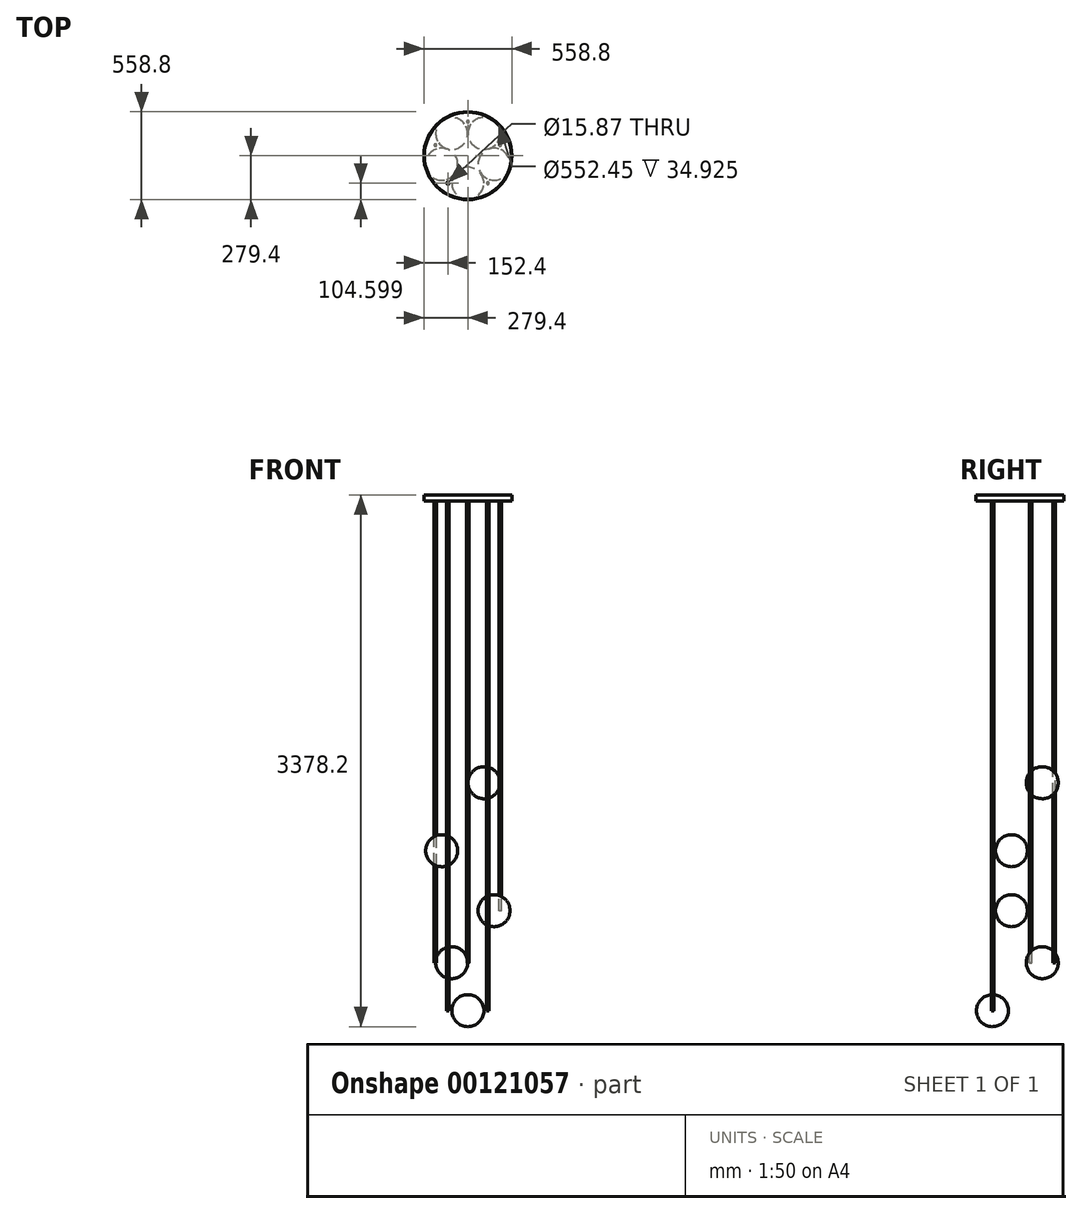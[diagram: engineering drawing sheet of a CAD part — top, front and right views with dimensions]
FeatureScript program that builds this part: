
annotation { "Feature Type Name" : "Feature", "Feature Type Description" : "" }
export const myFeature = defineFeature(function(context is Context, id is Id, definition is map)
    precondition{}
    {
        {
            var Q0;
            Q0=qCreatedBy(makeId("Front.planeOp"),FACE);
            var sketch = newSketch(context, id + "F0", { "sketchPlane" : qUnion([Q0])});
            skLineSegment(sketch, "E0", {"start": v(0, 0) * mm, "end": v(5560.38, 0) * mm, "construction": true});
            skCircle(sketch, "E1", {"center": v(0, 2108.2) * mm, "radius": 127 * mm});
            skLineSegment(sketch, "E2", {"start": v(0, 2235.2) * mm, "end": v(0, 4203.7) * mm});
            skLineSegment(sketch, "E3.bottom", {"start": v(0, 2540) * mm, "end": v(812.8, 2540) * mm});
            skLineSegment(sketch, "E3.top", {"start": v(0, 2489.2) * mm, "end": v(812.8, 2489.2) * mm});
            skLineSegment(sketch, "E3.left", {"start": v(0, 2540) * mm, "end": v(0, 2489.2) * mm});
            skLineSegment(sketch, "E3.right", {"start": v(812.8, 2540) * mm, "end": v(812.8, 2489.2) * mm});
            skLineSegment(sketch, "E4", {"start": v(812.8, 4203.7) * mm, "end": v(812.8, 1930.4) * mm});
            skCircle(sketch, "E5", {"center": v(939.8, 1930.4) * mm, "radius": 101.6 * mm});
            skLineSegment(sketch, "E6", {"start": v(1066.8, 4203.7) * mm, "end": v(1066.8, 1397) * mm});
            skLineSegment(sketch, "E7", {"start": v(812.8, 4203.7) * mm, "end": v(1066.8, 4203.7) * mm});
            skPoint(sketch, "E8", {"position": v(939.8, 4203.7) * mm});
            skCircle(sketch, "E9", {"center": v(939.8, 2819.4) * mm, "radius": 101.6 * mm});
            skCircle(sketch, "E10", {"center": v(1066.8, 1270) * mm, "radius": 127 * mm});
            skLineSegment(sketch, "E11.bottom", {"start": v(1066.8, 1701.8) * mm, "end": v(1879.6, 1701.8) * mm});
            skLineSegment(sketch, "E11.top", {"start": v(1066.8, 1651) * mm, "end": v(1879.6, 1651) * mm});
            skLineSegment(sketch, "E11.left", {"start": v(1066.8, 1701.8) * mm, "end": v(1066.8, 1651) * mm});
            skLineSegment(sketch, "E11.right", {"start": v(1879.6, 1701.8) * mm, "end": v(1879.6, 1651) * mm});
            skLineSegment(sketch, "E12", {"start": v(1879.6, 1651) * mm, "end": v(1879.6, 4203.7) * mm});
            skLineSegment(sketch, "E13", {"start": v(1879.6, 4203.7) * mm, "end": v(2133.6, 4203.7) * mm});
            skLineSegment(sketch, "E14", {"start": v(2133.6, 4203.7) * mm, "end": v(2133.6, 2362.2) * mm});
            skCircle(sketch, "E15", {"center": v(2006.6, 2362.2) * mm, "radius": 101.6 * mm});
            skPoint(sketch, "E15.centerSnap0", {"position": v(2006.6, 4203.7) * mm});
            skLineSegment(sketch, "E16", {"start": v(0, 4203.7) * mm, "end": v(0, 4267.2) * mm});
            skLineSegment(sketch, "E17", {"start": v(939.8, 2819.4) * mm, "end": v(812.8, 2819.4) * mm, "construction": true});
            skLineSegment(sketch, "E18", {"start": v(812.8, 2794) * mm, "end": v(939.8, 2794) * mm, "construction": true});
            skSolve(sketch);
        }
        {
            var Q0;
            Q0=qCreatedBy(makeId("Front.planeOp"),FACE);
            var sketch = newSketch(context, id + "F1", { "sketchPlane" : qUnion([Q0])});
            skLineSegment(sketch, "E19.0", {"start": v(0, 0) * mm, "end": v(5560.38, 0) * mm});
            skCircle(sketch, "E19.1", {"center": v(0, 2108.2) * mm, "radius": 127 * mm, "construction": true});
            skLineSegment(sketch, "E19.2", {"start": v(0, 2235.2) * mm, "end": v(0, 4203.7) * mm, "construction": true});
            skLineSegment(sketch, "E19.3", {"start": v(0, 2540) * mm, "end": v(812.8, 2540) * mm, "construction": true});
            skLineSegment(sketch, "E19.4", {"start": v(0, 2489.2) * mm, "end": v(812.8, 2489.2) * mm, "construction": true});
            skLineSegment(sketch, "E19.5", {"start": v(0, 2540) * mm, "end": v(0, 2489.2) * mm, "construction": true});
            skLineSegment(sketch, "E19.6", {"start": v(812.8, 2540) * mm, "end": v(812.8, 2489.2) * mm, "construction": true});
            skLineSegment(sketch, "E19.7", {"start": v(812.8, 4203.7) * mm, "end": v(812.8, 1930.4) * mm, "construction": true});
            skCircle(sketch, "E19.8", {"center": v(939.8, 1930.4) * mm, "radius": 101.6 * mm, "construction": true});
            skLineSegment(sketch, "E19.9", {"start": v(1066.8, 4203.7) * mm, "end": v(1066.8, 1397) * mm, "construction": true});
            skLineSegment(sketch, "E19.10", {"start": v(812.8, 4203.7) * mm, "end": v(1066.8, 4203.7) * mm, "construction": true});
            skPoint(sketch, "E19.11", {"position": v(939.8, 4203.7) * mm});
            skCircle(sketch, "E19.12", {"center": v(939.8, 2819.4) * mm, "radius": 101.6 * mm, "construction": true});
            skCircle(sketch, "E19.13", {"center": v(1066.8, 1270) * mm, "radius": 127 * mm, "construction": true});
            skLineSegment(sketch, "E19.14", {"start": v(1066.8, 1701.8) * mm, "end": v(1879.6, 1701.8) * mm, "construction": true});
            skLineSegment(sketch, "E19.15", {"start": v(1066.8, 1651) * mm, "end": v(1879.6, 1651) * mm, "construction": true});
            skLineSegment(sketch, "E19.16", {"start": v(1066.8, 1701.8) * mm, "end": v(1066.8, 1651) * mm, "construction": true});
            skLineSegment(sketch, "E19.17", {"start": v(1879.6, 1701.8) * mm, "end": v(1879.6, 1651) * mm, "construction": true});
            skLineSegment(sketch, "E19.18", {"start": v(1879.6, 1651) * mm, "end": v(1879.6, 4203.7) * mm, "construction": true});
            skLineSegment(sketch, "E19.19", {"start": v(1879.6, 4203.7) * mm, "end": v(2133.6, 4203.7) * mm, "construction": true});
            skLineSegment(sketch, "E19.20", {"start": v(2133.6, 4203.7) * mm, "end": v(2133.6, 2362.2) * mm, "construction": true});
            skCircle(sketch, "E19.21", {"center": v(2006.6, 2362.2) * mm, "radius": 101.6 * mm, "construction": true});
            skPoint(sketch, "E19.22", {"position": v(2006.6, 4203.7) * mm});
            skPoint(sketch, "E20.middle", {"position": v(0, 3219.45) * mm});
            skLineSegment(sketch, "E21.bottom", {"start": v(804.86, 4203.7) * mm, "end": v(820.74, 4203.7) * mm});
            skLineSegment(sketch, "E21.top", {"start": v(804.86, 2844.8) * mm, "end": v(820.74, 2844.8) * mm});
            skLineSegment(sketch, "E21.left", {"start": v(804.86, 4203.7) * mm, "end": v(804.86, 2844.8) * mm});
            skLineSegment(sketch, "E21.right", {"start": v(820.74, 4203.7) * mm, "end": v(820.74, 2844.8) * mm});
            skPoint(sketch, "E21.middle", {"position": v(812.8, 3524.25) * mm});
            skLineSegment(sketch, "E22.bottom", {"start": v(804.86, 2794) * mm, "end": v(820.74, 2794) * mm});
            skLineSegment(sketch, "E22.top", {"start": v(804.86, 2540) * mm, "end": v(820.74, 2540) * mm});
            skLineSegment(sketch, "E22.left", {"start": v(804.86, 2794) * mm, "end": v(804.86, 2540) * mm});
            skLineSegment(sketch, "E22.right", {"start": v(820.74, 2794) * mm, "end": v(820.74, 2540) * mm});
            skPoint(sketch, "E22.middle", {"position": v(812.8, 2667) * mm});
            skLineSegment(sketch, "E23", {"start": v(812.8, 2514.6) * mm, "end": v(0, 2514.6) * mm, "construction": true});
            skLineSegment(sketch, "E24.bottom", {"start": v(804.86, 2489.2) * mm, "end": v(820.74, 2489.2) * mm});
            skLineSegment(sketch, "E24.top", {"start": v(804.86, 1955.8) * mm, "end": v(820.74, 1955.8) * mm});
            skLineSegment(sketch, "E24.left", {"start": v(804.86, 2489.2) * mm, "end": v(804.86, 1955.8) * mm});
            skLineSegment(sketch, "E24.right", {"start": v(820.74, 2489.2) * mm, "end": v(820.74, 1955.8) * mm});
            skPoint(sketch, "E24.middle", {"position": v(812.8, 2222.5) * mm});
            skLineSegment(sketch, "E25", {"start": v(939.8, 1930.4) * mm, "end": v(812.8, 1930.4) * mm, "construction": true});
            skLineSegment(sketch, "E26", {"start": v(939.8, 1930.4) * mm, "end": v(1066.8, 1930.4) * mm, "construction": true});
            skLineSegment(sketch, "E27.bottom", {"start": v(1058.86, 4203.7) * mm, "end": v(1074.74, 4203.7) * mm});
            skLineSegment(sketch, "E27.top", {"start": v(1058.86, 2844.8) * mm, "end": v(1074.74, 2844.8) * mm});
            skLineSegment(sketch, "E27.left", {"start": v(1058.86, 4203.7) * mm, "end": v(1058.86, 2844.8) * mm});
            skLineSegment(sketch, "E27.right", {"start": v(1074.74, 4203.7) * mm, "end": v(1074.74, 2844.8) * mm});
            skPoint(sketch, "E27.middle", {"position": v(1066.8, 3524.25) * mm});
            skLineSegment(sketch, "E28.bottom", {"start": v(1058.86, 2794) * mm, "end": v(1074.74, 2794) * mm});
            skLineSegment(sketch, "E28.top", {"start": v(1058.86, 1955.8) * mm, "end": v(1074.74, 1955.8) * mm});
            skLineSegment(sketch, "E28.left", {"start": v(1058.86, 2794) * mm, "end": v(1058.86, 1955.8) * mm});
            skLineSegment(sketch, "E28.right", {"start": v(1074.74, 2794) * mm, "end": v(1074.74, 1955.8) * mm});
            skPoint(sketch, "E28.middle", {"position": v(1066.8, 2374.9) * mm});
            skLineSegment(sketch, "E29.bottom", {"start": v(1058.86, 1905) * mm, "end": v(1074.74, 1905) * mm});
            skLineSegment(sketch, "E29.top", {"start": v(1058.86, 1701.8) * mm, "end": v(1074.74, 1701.8) * mm});
            skLineSegment(sketch, "E29.left", {"start": v(1058.86, 1905) * mm, "end": v(1058.86, 1701.8) * mm});
            skLineSegment(sketch, "E29.right", {"start": v(1074.74, 1905) * mm, "end": v(1074.74, 1701.8) * mm});
            skPoint(sketch, "E29.middle", {"position": v(1066.8, 1803.4) * mm});
            skLineSegment(sketch, "E30", {"start": v(1066.8, 1676.4) * mm, "end": v(1879.6, 1676.4) * mm, "construction": true});
            skLineSegment(sketch, "E31.bottom", {"start": v(1058.86, 1651) * mm, "end": v(1074.74, 1651) * mm});
            skLineSegment(sketch, "E31.top", {"start": v(1058.86, 1397) * mm, "end": v(1074.74, 1397) * mm});
            skLineSegment(sketch, "E31.left", {"start": v(1058.86, 1651) * mm, "end": v(1058.86, 1397) * mm});
            skLineSegment(sketch, "E31.right", {"start": v(1074.74, 1651) * mm, "end": v(1074.74, 1397) * mm});
            skPoint(sketch, "E31.middle", {"position": v(1066.8, 1524) * mm});
            skLineSegment(sketch, "E32.bottom", {"start": v(1871.66, 4203.7) * mm, "end": v(1887.54, 4203.7) * mm});
            skLineSegment(sketch, "E32.top", {"start": v(1871.66, 2387.6) * mm, "end": v(1887.54, 2387.6) * mm});
            skLineSegment(sketch, "E32.left", {"start": v(1871.66, 4203.7) * mm, "end": v(1871.66, 2387.6) * mm});
            skLineSegment(sketch, "E32.right", {"start": v(1887.54, 4203.7) * mm, "end": v(1887.54, 2387.6) * mm});
            skPoint(sketch, "E32.middle", {"position": v(1879.6, 3295.65) * mm});
            skLineSegment(sketch, "E33.bottom", {"start": v(1871.66, 2336.8) * mm, "end": v(1887.54, 2336.8) * mm});
            skLineSegment(sketch, "E33.top", {"start": v(1871.66, 1701.8) * mm, "end": v(1887.54, 1701.8) * mm});
            skLineSegment(sketch, "E33.left", {"start": v(1871.66, 2336.8) * mm, "end": v(1871.66, 1701.8) * mm});
            skLineSegment(sketch, "E33.right", {"start": v(1887.54, 2336.8) * mm, "end": v(1887.54, 1701.8) * mm});
            skPoint(sketch, "E33.middle", {"position": v(1879.6, 2019.3) * mm});
            skLineSegment(sketch, "E34.bottom", {"start": v(2125.66, 4203.7) * mm, "end": v(2141.54, 4203.7) * mm});
            skLineSegment(sketch, "E34.top", {"start": v(2125.66, 2387.6) * mm, "end": v(2141.54, 2387.6) * mm});
            skLineSegment(sketch, "E34.left", {"start": v(2125.66, 4203.7) * mm, "end": v(2125.66, 2387.6) * mm});
            skLineSegment(sketch, "E34.right", {"start": v(2141.54, 4203.7) * mm, "end": v(2141.54, 2387.6) * mm});
            skPoint(sketch, "E34.middle", {"position": v(2133.6, 3295.65) * mm});
            skLineSegment(sketch, "E35.bottom", {"start": v(7.94, 4203.7) * mm, "end": v(-7.94, 4203.7) * mm});
            skLineSegment(sketch, "E35.top", {"start": v(7.94, 2540) * mm, "end": v(-7.94, 2540) * mm});
            skLineSegment(sketch, "E35.left", {"start": v(7.94, 4203.7) * mm, "end": v(7.94, 2540) * mm});
            skLineSegment(sketch, "E35.right", {"start": v(-7.94, 4203.7) * mm, "end": v(-7.94, 2540) * mm});
            skPoint(sketch, "E35.middle", {"position": v(0, 3371.85) * mm});
            skLineSegment(sketch, "E36.bottom", {"start": v(-7.94, 2489.2) * mm, "end": v(7.94, 2489.2) * mm});
            skLineSegment(sketch, "E36.top", {"start": v(-7.94, 2235.2) * mm, "end": v(7.94, 2235.2) * mm});
            skLineSegment(sketch, "E36.left", {"start": v(-7.94, 2489.2) * mm, "end": v(-7.94, 2235.2) * mm});
            skLineSegment(sketch, "E36.right", {"start": v(7.94, 2489.2) * mm, "end": v(7.94, 2235.2) * mm});
            skPoint(sketch, "E36.middle", {"position": v(0, 2362.2) * mm});
            skSolve(sketch);
        }
        {
            var Q0;
            Q0=qCreatedBy(makeId("Front.planeOp"),FACE);
            var sketch = newSketch(context, id + "F2", { "sketchPlane" : qUnion([Q0])});
            skLineSegment(sketch, "E37.0", {"start": v(0, 0) * mm, "end": v(5560.38, 0) * mm, "construction": true});
            skCircle(sketch, "E38", {"center": v(4419.6, 1524) * mm, "radius": 127 * mm, "construction": true});
            skLineSegment(sketch, "E39", {"start": v(4419.6, 1651) * mm, "end": v(4419.6, 4203.7) * mm, "construction": true});
            skLineSegment(sketch, "E40.0", {"start": v(1879.6, 4203.7) * mm, "end": v(2133.6, 4203.7) * mm, "construction": true});
            skLineSegment(sketch, "E41", {"start": v(4673.6, 4203.7) * mm, "end": v(4673.6, 2133.6) * mm, "construction": true});
            skLineSegment(sketch, "E42", {"start": v(4419.6, 4203.7) * mm, "end": v(4673.6, 4203.7) * mm, "construction": true});
            skCircle(sketch, "E43", {"center": v(4546.6, 2133.6) * mm, "radius": 101.6 * mm, "construction": true});
            skPoint(sketch, "E43.centerSnap0", {"position": v(4546.6, 4203.7) * mm});
            skLineSegment(sketch, "E44.bottom", {"start": v(4411.66, 4203.7) * mm, "end": v(4427.54, 4203.7) * mm});
            skLineSegment(sketch, "E44.top", {"start": v(4411.66, 2159) * mm, "end": v(4427.54, 2159) * mm});
            skLineSegment(sketch, "E44.left", {"start": v(4411.66, 4203.7) * mm, "end": v(4411.66, 2159) * mm});
            skLineSegment(sketch, "E44.right", {"start": v(4427.54, 4203.7) * mm, "end": v(4427.54, 2159) * mm});
            skPoint(sketch, "E44.middle", {"position": v(4419.6, 3181.35) * mm});
            skLineSegment(sketch, "E45.bottom", {"start": v(4411.66, 2108.2) * mm, "end": v(4427.54, 2108.2) * mm});
            skLineSegment(sketch, "E45.top", {"start": v(4411.66, 1651) * mm, "end": v(4427.54, 1651) * mm});
            skLineSegment(sketch, "E45.left", {"start": v(4411.66, 2108.2) * mm, "end": v(4411.66, 1651) * mm});
            skLineSegment(sketch, "E45.right", {"start": v(4427.54, 2108.2) * mm, "end": v(4427.54, 1651) * mm});
            skPoint(sketch, "E45.middle", {"position": v(4419.6, 1879.6) * mm});
            skCircle(sketch, "E46.0", {"center": v(2006.6, 2362.2) * mm, "radius": 101.6 * mm, "construction": true});
            skLineSegment(sketch, "E47.bottom", {"start": v(4665.66, 4203.7) * mm, "end": v(4681.54, 4203.7) * mm});
            skLineSegment(sketch, "E47.top", {"start": v(4665.66, 2159) * mm, "end": v(4681.54, 2159) * mm});
            skLineSegment(sketch, "E47.left", {"start": v(4665.66, 4203.7) * mm, "end": v(4665.66, 2159) * mm});
            skLineSegment(sketch, "E47.right", {"start": v(4681.54, 4203.7) * mm, "end": v(4681.54, 2159) * mm});
            skPoint(sketch, "E47.middle", {"position": v(4673.6, 3181.35) * mm});
            skSolve(sketch);
        }
        {
            var Q0;
            Q0=qCreatedBy(makeId("Front.planeOp"),FACE);
            var sketch = newSketch(context, id + "F3", { "sketchPlane" : qUnion([Q0])});
            skLineSegment(sketch, "E48.0", {"start": v(0, 0) * mm, "end": v(5560.38, 0) * mm, "construction": true});
            skLineSegment(sketch, "E49", {"start": v(5560.38, 0) * mm, "end": v(9395.47, 0) * mm, "construction": true});
            skCircle(sketch, "E50", {"center": v(7086.6, 965.2) * mm, "radius": 101.6 * mm, "construction": true});
            skCircle(sketch, "E51.0", {"center": v(4419.6, 1524) * mm, "radius": 127 * mm, "construction": true});
            skLineSegment(sketch, "E52.0", {"start": v(4419.6, 4203.7) * mm, "end": v(4673.6, 4203.7) * mm, "construction": true});
            skLineSegment(sketch, "E53", {"start": v(7086.6, 965.2) * mm, "end": v(6959.6, 965.2) * mm, "construction": true});
            skLineSegment(sketch, "E54", {"start": v(6959.6, 965.2) * mm, "end": v(6959.6, 4203.7) * mm, "construction": true});
            skLineSegment(sketch, "E55", {"start": v(7213.6, 965.2) * mm, "end": v(7213.6, 4203.7) * mm, "construction": true});
            skLineSegment(sketch, "E56", {"start": v(6959.6, 4203.7) * mm, "end": v(7213.6, 4203.7) * mm, "construction": true});
            skPoint(sketch, "E57", {"position": v(7086.6, 4203.7) * mm});
            skLineSegment(sketch, "E58", {"start": v(6959.6, 4203.7) * mm, "end": v(6705.6, 4203.7) * mm, "construction": true});
            skLineSegment(sketch, "E59", {"start": v(6705.6, 4203.7) * mm, "end": v(6705.6, 1981.2) * mm, "construction": true});
            skCircle(sketch, "E60", {"center": v(6832.6, 1981.2) * mm, "radius": 101.6 * mm, "construction": true});
            skPoint(sketch, "E60.centerSnap0", {"position": v(6832.6, 4203.7) * mm});
            skLineSegment(sketch, "E61", {"start": v(6705.6, 4203.7) * mm, "end": v(6451.6, 4203.7) * mm, "construction": true});
            skLineSegment(sketch, "E62", {"start": v(6451.6, 4203.7) * mm, "end": v(6451.6, 1270) * mm, "construction": true});
            skCircle(sketch, "E63", {"center": v(6578.6, 1270) * mm, "radius": 101.6 * mm, "construction": true});
            skPoint(sketch, "E63.centerSnap0", {"position": v(6578.6, 4203.7) * mm});
            skLineSegment(sketch, "E64", {"start": v(7213.6, 4203.7) * mm, "end": v(7467.6, 4203.7) * mm, "construction": true});
            skLineSegment(sketch, "E65", {"start": v(7467.6, 4203.7) * mm, "end": v(7467.6, 1600.2) * mm, "construction": true});
            skLineSegment(sketch, "E66", {"start": v(7467.6, 4203.7) * mm, "end": v(7721.6, 4203.7) * mm});
            skLineSegment(sketch, "E67", {"start": v(7721.6, 4203.7) * mm, "end": v(7721.6, 2413) * mm, "construction": true});
            skCircle(sketch, "E68", {"center": v(7594.6, 2413) * mm, "radius": 101.6 * mm, "construction": true});
            skPoint(sketch, "E68.centerSnap0", {"position": v(7594.6, 4203.7) * mm});
            skCircle(sketch, "E69", {"center": v(7340.6, 1600.2) * mm, "radius": 101.6 * mm, "construction": true});
            skPoint(sketch, "E69.centerSnap0", {"position": v(7340.6, 4203.7) * mm});
            skLineSegment(sketch, "E70", {"start": v(6705.6, 1981.2) * mm, "end": v(6705.6, 1270) * mm, "construction": true});
            skLineSegment(sketch, "E71", {"start": v(7467.6, 2413) * mm, "end": v(7467.6, 1600.2) * mm, "construction": true});
            skLineSegment(sketch, "E72", {"start": v(7086.6, 863.6) * mm, "end": v(8026.4, 863.6) * mm, "construction": true});
            skLineSegment(sketch, "E73", {"start": v(8026.4, 863.6) * mm, "end": v(8026.4, 4203.7) * mm, "construction": true});
            skSolve(sketch);
        }
        {
            var Q0;
            Q0=qCreatedBy(makeId("Top.planeOp"),FACE);
            var Q1;
            Q1=sQuery(id+"F3.wireOp",VERTEX,"E57");
            cPlane(context, id + "F4", {"entities" : qUnion([Q0, Q1]), "cplaneType" : CPlaneType.PLANE_POINT, "offset" : 25.4 * mm, "width" : 152.4 * mm, "height" : 152.4 * mm});
        }
        {
            var Q0;
            Q0=qCreatedBy(id+"F4.planeOp",FACE);
            var sketch = newSketch(context, id + "F5", { "sketchPlane" : qUnion([Q0])});
            skPoint(sketch, "E74.0", {"position": v(7086.6, 0) * mm});
            skCircle(sketch, "E75.cCircle", {"center": v(7086.6, 0) * mm, "radius": 174.8 * mm, "construction": true});
            skLineSegment(sketch, "E75.0", {"start": v(7086.6, 216.07) * mm, "end": v(7292.1, 66.77) * mm});
            skLineSegment(sketch, "E75.1", {"start": v(7292.1, 66.77) * mm, "end": v(7213.6, -174.8) * mm});
            skLineSegment(sketch, "E75.2", {"start": v(7213.6, -174.8) * mm, "end": v(6959.6, -174.8) * mm});
            skLineSegment(sketch, "E75.3", {"start": v(6959.6, -174.8) * mm, "end": v(6881.1, 66.77) * mm});
            skLineSegment(sketch, "E75.4", {"start": v(6881.1, 66.77) * mm, "end": v(7086.6, 216.07) * mm});
            skPoint(sketch, "E75.0.midPoint", {"position": v(7189.35, 141.42) * mm});
            skLineSegment(sketch, "E76.0", {"start": v(6959.6, 0) * mm, "end": v(7213.6, 0) * mm, "construction": true});
            skSolve(sketch);
        }
        {
            var Q0;
            Q0=qCreatedBy(id+"F4.planeOp",FACE);
            var Q1;
            Q1=sQuery(id+"F3.wireOp",VERTEX,"E55.start");
            cPlane(context, id + "F6", {"entities" : qUnion([Q0, Q1]), "cplaneType" : CPlaneType.PLANE_POINT, "offset" : 25.4 * mm, "width" : 152.4 * mm, "height" : 152.4 * mm});
        }
        {
            var Q0;
            Q0=qCreatedBy(id+"F4.planeOp",FACE);
            var sketch = newSketch(context, id + "F7", { "sketchPlane" : qUnion([Q0])});
            skLineSegment(sketch, "E77.0", {"start": v(6881.1, 66.77) * mm, "end": v(7086.6, 216.07) * mm, "construction": true});
            skLineSegment(sketch, "E77.1", {"start": v(7086.6, 216.07) * mm, "end": v(7292.1, 66.77) * mm, "construction": true});
            skLineSegment(sketch, "E77.2", {"start": v(7292.1, 66.77) * mm, "end": v(7213.6, -174.8) * mm, "construction": true});
            skLineSegment(sketch, "E77.3", {"start": v(7213.6, -174.8) * mm, "end": v(6959.6, -174.8) * mm, "construction": true});
            skLineSegment(sketch, "E77.4", {"start": v(6959.6, -174.8) * mm, "end": v(6881.1, 66.77) * mm, "construction": true});
            skCircle(sketch, "E78", {"center": v(7213.6, -174.8) * mm, "radius": 7.94 * mm});
            skCircle(sketch, "E79", {"center": v(6959.6, -174.8) * mm, "radius": 7.94 * mm});
            skCircle(sketch, "E80", {"center": v(6881.1, 66.77) * mm, "radius": 7.94 * mm});
            skCircle(sketch, "E81", {"center": v(7086.6, 216.07) * mm, "radius": 7.94 * mm});
            skCircle(sketch, "E82", {"center": v(7292.1, 66.77) * mm, "radius": 7.94 * mm});
            skSolve(sketch);
        }
        {
            var Q0;
            Q0=makeQuery(id+"F7.imprint","IMPRINT",FACE,{"disambiguationData":[TD([[makeQuery(id+"F7.imprint","IMPRINT",EDGE,{"derivedFrom":sQuery(id+"F7.wireOp",EDGE,"E78")}),1.0]])]});
            var Q1;
            Q1=makeQuery(id+"F7.imprint","IMPRINT",FACE,{"disambiguationData":[TD([[makeQuery(id+"F7.imprint","IMPRINT",EDGE,{"derivedFrom":sQuery(id+"F7.wireOp",EDGE,"E79")}),1.0]])]});
            var Q2;
            Q2=qCreatedBy(id+"F6.planeOp",FACE);
            extrude(context, id + "F8", {"entities" : qUnion([Q0, Q1]), "endBound" : BoundingType.UP_TO_SURFACE, "oppositeDirection" : true, "endBoundEntityFace" : qUnion([Q2]), "depth" : 25.4 * mm});
        }
        {
            var Q0;
            Q0=makeQuery(id+"F5.imprint","IMPRINT",FACE,{"disambiguationData":[TD([[makeQuery(id+"F5.imprint","IMPRINT",EDGE,{"derivedFrom":sQuery(id+"F5.wireOp",EDGE,"E75.0")}),-1.0]])]});
            var Q1;
            Q1=sQuery(id+"F3.wireOp",VERTEX,"E60.center");
            cPlane(context, id + "F9", {"entities" : qUnion([Q0, Q1]), "cplaneType" : CPlaneType.PLANE_POINT, "offset" : 25.4 * mm, "width" : 152.4 * mm, "height" : 152.4 * mm});
        }
        {
            var Q0;
            Q0=qCreatedBy(id+"F9.planeOp",FACE);
            var Q1;
            Q1=sQuery(id+"F3.wireOp",VERTEX,"E63.center");
            cPlane(context, id + "F10", {"entities" : qUnion([Q0, Q1]), "cplaneType" : CPlaneType.PLANE_POINT, "offset" : 25.4 * mm, "width" : 152.4 * mm, "height" : 152.4 * mm});
        }
        {
            var Q0;
            Q0=qCreatedBy(id+"F9.planeOp",FACE);
            var Q1;
            Q1=sQuery(id+"F3.wireOp",VERTEX,"E69.center");
            cPlane(context, id + "F11", {"entities" : qUnion([Q0, Q1]), "cplaneType" : CPlaneType.PLANE_POINT, "offset" : 25.4 * mm, "width" : 152.4 * mm, "height" : 152.4 * mm});
        }
        {
            var Q0;
            Q0=qCreatedBy(id+"F11.planeOp",FACE);
            var Q1;
            Q1=sQuery(id+"F3.wireOp",VERTEX,"E68.center");
            cPlane(context, id + "F12", {"entities" : qUnion([Q0, Q1]), "cplaneType" : CPlaneType.PLANE_POINT, "offset" : 25.4 * mm, "width" : 152.4 * mm, "height" : 152.4 * mm});
        }
        {
            var Q0;
            Q0=makeQuery(id+"F7.imprint","IMPRINT",FACE,{"disambiguationData":[TD([[makeQuery(id+"F7.imprint","IMPRINT",EDGE,{"derivedFrom":sQuery(id+"F7.wireOp",EDGE,"E80")}),1.0]])]});
            var Q1;
            Q1=makeQuery(id+"F7.imprint","IMPRINT",FACE,{"disambiguationData":[TD([[makeQuery(id+"F7.imprint","IMPRINT",EDGE,{"derivedFrom":sQuery(id+"F7.wireOp",EDGE,"E81")}),1.0]])]});
            var Q2;
            Q2=qCreatedBy(id+"F10.planeOp",FACE);
            extrude(context, id + "F13", {"entities" : qUnion([Q0, Q1]), "endBound" : BoundingType.UP_TO_SURFACE, "oppositeDirection" : true, "endBoundEntityFace" : qUnion([Q2]), "depth" : 25.4 * mm});
        }
        {
            var Q0;
            Q0=makeQuery(id+"F7.imprint","IMPRINT",FACE,{"disambiguationData":[TD([[makeQuery(id+"F7.imprint","IMPRINT",EDGE,{"derivedFrom":sQuery(id+"F7.wireOp",EDGE,"E82")}),1.0]])]});
            var Q1;
            Q1=qCreatedBy(id+"F11.planeOp",FACE);
            extrude(context, id + "F14", {"entities" : qUnion([Q0]), "endBound" : BoundingType.UP_TO_SURFACE, "oppositeDirection" : true, "endBoundEntityFace" : qUnion([Q1]), "depth" : 25.4 * mm});
        }
        {
            var Q0;
            Q0=qCreatedBy(id+"F6.planeOp",FACE);
            var sketch = newSketch(context, id + "F15", { "sketchPlane" : qUnion([Q0])});
            skLineSegment(sketch, "E83.0", {"start": v(7213.6, -174.8) * mm, "end": v(6959.6, -174.8) * mm});
            skArc(sketch, "E84", {"start": v(6985, -174.8) * mm, "mid": v(7086.6, -276.4) * mm, "end": v(7188.2, -174.8) * mm});
            skSolve(sketch);
        }
        {
            var Q0;
            Q0 = qSketchRegion(id + "F15", true);
            var Q1;
            Q1=sQuery(id+"F15.wireOp",EDGE,"E83.0");
            revolve(context, id + "F16", {"entities" : qUnion([Q0]), "axis" : qUnion([Q1]), "revolveType" : RevolveType.FULL});
        }
        {
            var Q0;
            Q0=qCreatedBy(id+"F9.planeOp",FACE);
            var sketch = newSketch(context, id + "F17", { "sketchPlane" : qUnion([Q0])});
            skLineSegment(sketch, "E85.0", {"start": v(6959.6, -174.8) * mm, "end": v(6881.1, 66.77) * mm});
            skArc(sketch, "E86", {"start": v(6888.96, 42.61) * mm, "mid": v(6823.73, -85.41) * mm, "end": v(6951.75, -150.64) * mm});
            skSolve(sketch);
        }
        {
            var Q0;
            Q0 = qSketchRegion(id + "F17", true);
            var Q1;
            Q1=sQuery(id+"F17.wireOp",EDGE,"E85.0");
            revolve(context, id + "F18", {"entities" : qUnion([Q0]), "axis" : qUnion([Q1]), "revolveType" : RevolveType.FULL});
        }
        {
            var Q0;
            Q0=qCreatedBy(id+"F10.planeOp",FACE);
            var sketch = newSketch(context, id + "F19", { "sketchPlane" : qUnion([Q0])});
            skLineSegment(sketch, "E87.0", {"start": v(6881.1, 66.77) * mm, "end": v(7086.6, 216.07) * mm});
            skArc(sketch, "E88", {"start": v(7066.05, 201.14) * mm, "mid": v(6924.14, 223.61) * mm, "end": v(6901.66, 81.7) * mm});
            skSolve(sketch);
        }
        {
            var Q0;
            Q0 = qSketchRegion(id + "F19", true);
            var Q1;
            Q1=sQuery(id+"F19.wireOp",EDGE,"E87.0");
            revolve(context, id + "F20", {"entities" : qUnion([Q0]), "axis" : qUnion([Q1]), "revolveType" : RevolveType.FULL});
        }
        {
            var Q0;
            Q0=qCreatedBy(id+"F12.planeOp",FACE);
            var sketch = newSketch(context, id + "F21", { "sketchPlane" : qUnion([Q0])});
            skLineSegment(sketch, "E89.0", {"start": v(7086.6, 216.07) * mm, "end": v(7292.1, 66.77) * mm});
            skArc(sketch, "E90", {"start": v(7271.54, 81.7) * mm, "mid": v(7249.06, 223.61) * mm, "end": v(7107.15, 201.14) * mm});
            skSolve(sketch);
        }
        {
            var Q0;
            Q0 = qSketchRegion(id + "F21", true);
            var Q1;
            Q1=sQuery(id+"F21.wireOp",EDGE,"E89.0");
            revolve(context, id + "F22", {"entities" : qUnion([Q0]), "axis" : qUnion([Q1]), "revolveType" : RevolveType.FULL});
        }
        {
            var Q0;
            Q0=qCreatedBy(id+"F11.planeOp",FACE);
            var sketch = newSketch(context, id + "F23", { "sketchPlane" : qUnion([Q0])});
            skLineSegment(sketch, "E91.0", {"start": v(7292.1, 66.77) * mm, "end": v(7213.6, -174.8) * mm});
            skArc(sketch, "E92", {"start": v(7221.45, -150.64) * mm, "mid": v(7349.47, -85.41) * mm, "end": v(7284.24, 42.61) * mm});
            skSolve(sketch);
        }
        {
            var Q0;
            Q0 = qSketchRegion(id + "F23", true);
            var Q1;
            Q1=sQuery(id+"F23.wireOp",EDGE,"E91.0");
            revolve(context, id + "F24", {"surfaceOperationType" : NewSurfaceOperationType.NEW, "entities" : qUnion([Q0]), "axis" : qUnion([Q1]), "revolveType" : RevolveType.FULL});
        }
        {
            var Q0;
            Q0=qCreatedBy(makeId("Front.planeOp"),FACE);
            var sketch = newSketch(context, id + "F25", { "sketchPlane" : qUnion([Q0])});
            skLineSegment(sketch, "E93.0", {"start": v(0, 0) * mm, "end": v(5560.38, 0) * mm});
            skLineSegment(sketch, "E93.1", {"start": v(5560.38, 0) * mm, "end": v(9395.47, 0) * mm});
            skCircle(sketch, "E93.2", {"center": v(7086.6, 965.2) * mm, "radius": 101.6 * mm, "construction": true});
            skCircle(sketch, "E93.3", {"center": v(4419.6, 1524) * mm, "radius": 127 * mm});
            skLineSegment(sketch, "E93.4", {"start": v(4419.6, 4203.7) * mm, "end": v(4673.6, 4203.7) * mm});
            skLineSegment(sketch, "E93.5", {"start": v(7086.6, 965.2) * mm, "end": v(6959.6, 965.2) * mm, "construction": true});
            skLineSegment(sketch, "E93.6", {"start": v(6959.6, 965.2) * mm, "end": v(6959.6, 4203.7) * mm, "construction": true});
            skLineSegment(sketch, "E93.7", {"start": v(7213.6, 965.2) * mm, "end": v(7213.6, 4203.7) * mm, "construction": true});
            skLineSegment(sketch, "E93.8", {"start": v(6959.6, 4203.7) * mm, "end": v(7213.6, 4203.7) * mm, "construction": true});
            skPoint(sketch, "E93.9", {"position": v(7086.6, 4203.7) * mm});
            skLineSegment(sketch, "E93.10", {"start": v(6959.6, 4203.7) * mm, "end": v(6705.6, 4203.7) * mm, "construction": true});
            skLineSegment(sketch, "E93.11", {"start": v(6705.6, 4203.7) * mm, "end": v(6705.6, 1981.2) * mm, "construction": true});
            skCircle(sketch, "E93.12", {"center": v(6832.6, 1981.2) * mm, "radius": 101.6 * mm, "construction": true});
            skPoint(sketch, "E93.13", {"position": v(6832.6, 4203.7) * mm});
            skLineSegment(sketch, "E93.14", {"start": v(6705.6, 4203.7) * mm, "end": v(6451.6, 4203.7) * mm, "construction": true});
            skLineSegment(sketch, "E93.15", {"start": v(6451.6, 4203.7) * mm, "end": v(6451.6, 1270) * mm, "construction": true});
            skCircle(sketch, "E93.16", {"center": v(6578.6, 1270) * mm, "radius": 101.6 * mm, "construction": true});
            skPoint(sketch, "E93.17", {"position": v(6578.6, 4203.7) * mm});
            skLineSegment(sketch, "E93.18", {"start": v(7213.6, 4203.7) * mm, "end": v(7467.6, 4203.7) * mm, "construction": true});
            skLineSegment(sketch, "E93.19", {"start": v(7467.6, 4203.7) * mm, "end": v(7467.6, 1600.2) * mm, "construction": true});
            skLineSegment(sketch, "E93.20", {"start": v(7467.6, 4203.7) * mm, "end": v(7721.6, 4203.7) * mm, "construction": true});
            skLineSegment(sketch, "E93.21", {"start": v(7721.6, 4203.7) * mm, "end": v(7721.6, 2413) * mm, "construction": true});
            skCircle(sketch, "E93.22", {"center": v(7594.6, 2413) * mm, "radius": 101.6 * mm, "construction": true});
            skPoint(sketch, "E93.23", {"position": v(7594.6, 4203.7) * mm});
            skCircle(sketch, "E93.24", {"center": v(7340.6, 1600.2) * mm, "radius": 101.6 * mm, "construction": true});
            skPoint(sketch, "E93.25", {"position": v(7340.6, 4203.7) * mm});
            skLineSegment(sketch, "E93.26", {"start": v(6705.6, 1981.2) * mm, "end": v(6705.6, 1270) * mm, "construction": true});
            skLineSegment(sketch, "E93.27", {"start": v(7467.6, 2413) * mm, "end": v(7467.6, 1600.2) * mm, "construction": true});
            skLineSegment(sketch, "E94.bottom", {"start": v(6459.54, 4203.7) * mm, "end": v(6443.66, 4203.7) * mm});
            skLineSegment(sketch, "E94.top", {"start": v(6459.54, 2438.4) * mm, "end": v(6443.66, 2438.4) * mm});
            skLineSegment(sketch, "E94.left", {"start": v(6459.54, 4203.7) * mm, "end": v(6459.54, 2438.4) * mm});
            skLineSegment(sketch, "E94.right", {"start": v(6443.66, 4203.7) * mm, "end": v(6443.66, 2438.4) * mm});
            skPoint(sketch, "E94.middle", {"position": v(6451.6, 3321.05) * mm});
            skLineSegment(sketch, "E95.bottom", {"start": v(6713.54, 4203.7) * mm, "end": v(6697.66, 4203.7) * mm});
            skLineSegment(sketch, "E95.top", {"start": v(6713.54, 2006.6) * mm, "end": v(6697.66, 2006.6) * mm});
            skLineSegment(sketch, "E95.left", {"start": v(6713.54, 4203.7) * mm, "end": v(6713.54, 2006.6) * mm});
            skLineSegment(sketch, "E95.right", {"start": v(6697.66, 4203.7) * mm, "end": v(6697.66, 2006.6) * mm});
            skPoint(sketch, "E95.middle", {"position": v(6705.6, 3105.15) * mm});
            skLineSegment(sketch, "E96.bottom", {"start": v(6697.66, 1955.8) * mm, "end": v(6713.54, 1955.8) * mm});
            skLineSegment(sketch, "E96.top", {"start": v(6697.66, 1295.4) * mm, "end": v(6713.54, 1295.4) * mm});
            skLineSegment(sketch, "E96.left", {"start": v(6697.66, 1955.8) * mm, "end": v(6697.66, 1295.4) * mm});
            skLineSegment(sketch, "E96.right", {"start": v(6713.54, 1955.8) * mm, "end": v(6713.54, 1295.4) * mm});
            skPoint(sketch, "E96.middle", {"position": v(6705.6, 1625.6) * mm});
            skLineSegment(sketch, "E97.bottom", {"start": v(6967.54, 4203.7) * mm, "end": v(6951.66, 4203.7) * mm});
            skLineSegment(sketch, "E97.top", {"start": v(6967.54, 2006.6) * mm, "end": v(6951.66, 2006.6) * mm});
            skLineSegment(sketch, "E97.left", {"start": v(6967.54, 4203.7) * mm, "end": v(6967.54, 2006.6) * mm});
            skLineSegment(sketch, "E97.right", {"start": v(6951.66, 4203.7) * mm, "end": v(6951.66, 2006.6) * mm});
            skPoint(sketch, "E97.middle", {"position": v(6959.6, 3105.15) * mm});
            skLineSegment(sketch, "E98.bottom", {"start": v(6967.54, 1955.8) * mm, "end": v(6951.66, 1955.8) * mm});
            skLineSegment(sketch, "E98.top", {"start": v(6967.54, 990.6) * mm, "end": v(6951.66, 990.6) * mm});
            skLineSegment(sketch, "E98.left", {"start": v(6967.54, 1955.8) * mm, "end": v(6967.54, 990.6) * mm});
            skLineSegment(sketch, "E98.right", {"start": v(6951.66, 1955.8) * mm, "end": v(6951.66, 990.6) * mm});
            skPoint(sketch, "E98.middle", {"position": v(6959.6, 1473.2) * mm});
            skLineSegment(sketch, "E99.bottom", {"start": v(7205.66, 4203.7) * mm, "end": v(7221.54, 4203.7) * mm});
            skLineSegment(sketch, "E99.top", {"start": v(7205.66, 1625.6) * mm, "end": v(7221.54, 1625.6) * mm});
            skLineSegment(sketch, "E99.left", {"start": v(7205.66, 4203.7) * mm, "end": v(7205.66, 1625.6) * mm});
            skLineSegment(sketch, "E99.right", {"start": v(7221.54, 4203.7) * mm, "end": v(7221.54, 1625.6) * mm});
            skPoint(sketch, "E99.middle", {"position": v(7213.6, 2914.65) * mm});
            skLineSegment(sketch, "E100.bottom", {"start": v(7205.66, 1574.8) * mm, "end": v(7221.54, 1574.8) * mm});
            skLineSegment(sketch, "E100.top", {"start": v(7205.66, 990.6) * mm, "end": v(7221.54, 990.6) * mm});
            skLineSegment(sketch, "E100.left", {"start": v(7205.66, 1574.8) * mm, "end": v(7205.66, 990.6) * mm});
            skLineSegment(sketch, "E100.right", {"start": v(7221.54, 1574.8) * mm, "end": v(7221.54, 990.6) * mm});
            skPoint(sketch, "E100.middle", {"position": v(7213.6, 1282.7) * mm});
            skLineSegment(sketch, "E101.bottom", {"start": v(7459.66, 4203.7) * mm, "end": v(7475.54, 4203.7) * mm});
            skLineSegment(sketch, "E101.top", {"start": v(7459.66, 1625.6) * mm, "end": v(7475.54, 1625.6) * mm});
            skLineSegment(sketch, "E101.left", {"start": v(7459.66, 4203.7) * mm, "end": v(7459.66, 2438.4) * mm});
            skLineSegment(sketch, "E101.right", {"start": v(7475.54, 4203.7) * mm, "end": v(7475.54, 2438.4) * mm});
            skPoint(sketch, "E101.middle", {"position": v(7467.6, 2914.65) * mm});
            skLineSegment(sketch, "E102.bottom", {"start": v(7459.66, 1574.8) * mm, "end": v(7475.54, 1574.8) * mm});
            skLineSegment(sketch, "E102.top", {"start": v(7459.66, 2438.4) * mm, "end": v(7475.54, 2438.4) * mm});
            skLineSegment(sketch, "E102.left", {"start": v(7459.66, 2387.6) * mm, "end": v(7459.66, 1574.8) * mm});
            skLineSegment(sketch, "E102.right", {"start": v(7475.54, 2387.6) * mm, "end": v(7475.54, 1574.8) * mm});
            skPoint(sketch, "E102.middle", {"position": v(7467.6, 2006.6) * mm});
            skLineSegment(sketch, "E103.bottom", {"start": v(7713.66, 4203.7) * mm, "end": v(7729.54, 4203.7) * mm});
            skLineSegment(sketch, "E103.top", {"start": v(7713.66, 2438.4) * mm, "end": v(7729.54, 2438.4) * mm});
            skLineSegment(sketch, "E103.left", {"start": v(7713.66, 4203.7) * mm, "end": v(7713.66, 2438.4) * mm, "construction": true});
            skLineSegment(sketch, "E103.right", {"start": v(7729.54, 4203.7) * mm, "end": v(7729.54, 2438.4) * mm, "construction": true});
            skPoint(sketch, "E103.middle", {"position": v(7721.6, 3321.05) * mm});
            skLineSegment(sketch, "E104", {"start": v(7713.66, 2438.4) * mm, "end": v(6514.3, 2438.4) * mm, "construction": true});
            skLineSegment(sketch, "E105.0", {"start": v(7713.66, 2387.6) * mm, "end": v(6518.9, 2387.6) * mm, "construction": true});
            skLineSegment(sketch, "E106.bottom", {"start": v(6443.66, 2387.6) * mm, "end": v(6459.54, 2387.6) * mm});
            skLineSegment(sketch, "E106.top", {"start": v(6443.66, 1295.4) * mm, "end": v(6459.54, 1295.4) * mm});
            skLineSegment(sketch, "E106.left", {"start": v(6443.66, 2387.6) * mm, "end": v(6443.66, 1295.4) * mm});
            skLineSegment(sketch, "E106.right", {"start": v(6459.54, 2387.6) * mm, "end": v(6459.54, 1295.4) * mm});
            skPoint(sketch, "E106.middle", {"position": v(6451.6, 1841.5) * mm});
            skLineSegment(sketch, "E107.trimOffspring", {"start": v(7475.54, 2387.6) * mm, "end": v(7475.54, 1625.6) * mm});
            skLineSegment(sketch, "E108.trimOffspring", {"start": v(7459.66, 2387.6) * mm, "end": v(7459.66, 1625.6) * mm});
            skSolve(sketch);
        }
        {
            var Q0;
            Q0 = qSketchRegion(id + "F23", true);
            var Q1;
            Q1=sQuery(id+"F23.wireOp",EDGE,"E91.0");
            revolve(context, id + "F26", {"entities" : qUnion([Q0]), "axis" : qUnion([Q1]), "revolveType" : RevolveType.FULL});
        }
        {
            var Q0;
            Q0=makeQuery(id+"F8.opExtrude","CAP_FACE",FACE,{"disambiguationData":[OSD([sQuery(id+"F7.wireOp",EDGE,"E79")])],"isStart":true});
            var sketch = newSketch(context, id + "F27", { "sketchPlane" : qUnion([Q0])});
            skLineSegment(sketch, "E109.0", {"start": v(6881.1, 66.77) * mm, "end": v(7086.6, 216.07) * mm, "construction": true});
            skLineSegment(sketch, "E109.1", {"start": v(6959.6, -174.8) * mm, "end": v(6881.1, 66.77) * mm, "construction": true});
            skLineSegment(sketch, "E109.2", {"start": v(7213.6, -174.8) * mm, "end": v(6959.6, -174.8) * mm, "construction": true});
            skLineSegment(sketch, "E109.3", {"start": v(7292.1, 66.77) * mm, "end": v(7213.6, -174.8) * mm, "construction": true});
            skLineSegment(sketch, "E109.4", {"start": v(7086.6, 216.07) * mm, "end": v(7292.1, 66.77) * mm, "construction": true});
            skPoint(sketch, "E109.5", {"position": v(7086.6, 0) * mm});
            skCircle(sketch, "E110", {"center": v(7086.6, 0) * mm, "radius": 279.4 * mm});
            skCircle(sketch, "E111.0", {"center": v(6959.6, -174.8) * mm, "radius": 7.94 * mm, "construction": true});
            skSolve(sketch);
        }
        {
            var Q0;
            Q0=makeQuery(id+"F27.imprint","IMPRINT",FACE,{"disambiguationData":[TD([[makeQuery(id+"F27.imprint","IMPRINT",EDGE,{"derivedFrom":sQuery(id+"F27.wireOp",EDGE,"E110")}),1.0]])]});
            extrude(context, id + "F28", {"entities" : qUnion([Q0]), "depth" : 38.1 * mm, "offsetDistance" : 25.4 * mm});
        }
        {
            var Q0;
            Q0=makeQuery(id+"F28.opExtrude","CAP_FACE",FACE,{"disambiguationData":[OSD([sQuery(id+"F7.wireOp",EDGE,"E79"),sQuery(id+"F27.wireOp",EDGE,"E110")])],"isStart":false});
            var sketch = newSketch(context, id + "F29", { "sketchPlane" : qUnion([Q0])});
            skCircle(sketch, "E112.0", {"center": v(7086.6, 0) * mm, "radius": 279.4 * mm, "construction": true});
            skCircle(sketch, "E113.0", {"center": v(7086.6, 0) * mm, "radius": 276.23 * mm});
            skSolve(sketch);
        }
        {
            var Q0;
            Q0 = qSketchRegion(id + "F29", true);
            extrude(context, id + "F30", {"entities" : qUnion([Q0]), "operationType" : NewBodyOperationType.REMOVE, "oppositeDirection" : true, "depth" : 34.92 * mm, "offsetDistance" : 25.4 * mm});
        }
    });
